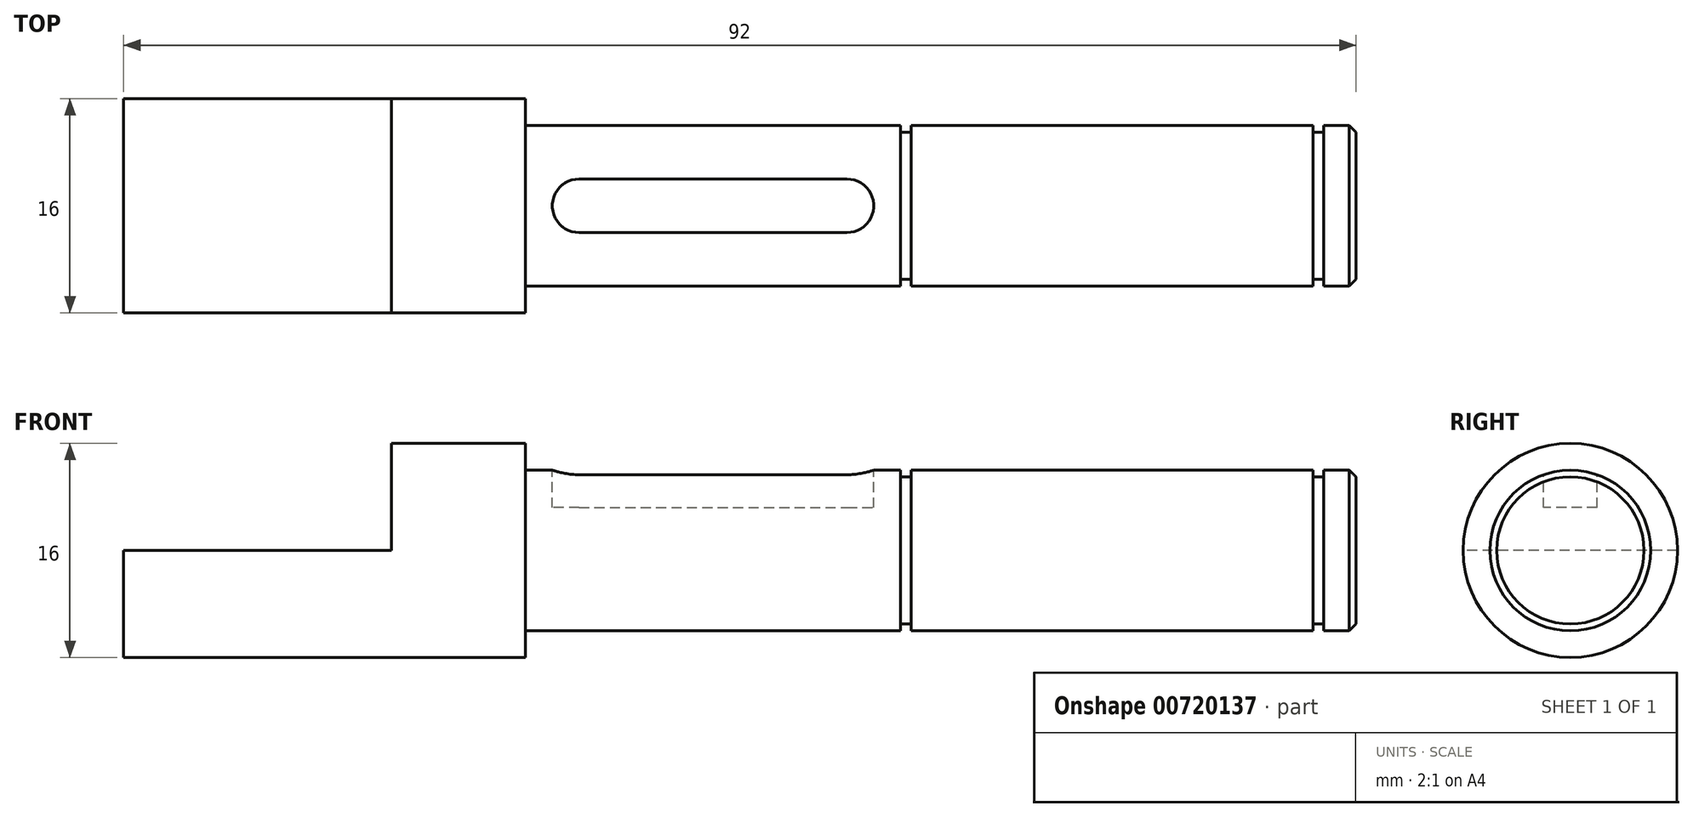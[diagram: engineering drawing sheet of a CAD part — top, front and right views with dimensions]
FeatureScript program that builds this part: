
annotation { "Feature Type Name" : "Feature", "Feature Type Description" : "" }
export const myFeature = defineFeature(function(context is Context, id is Id, definition is map)
    precondition{}
    {
        {
            var Q0;
            Q0=qCreatedBy(makeId("Front.planeOp"),FACE);
            var sketch = newSketch(context, id + "F0", { "sketchPlane" : qUnion([Q0])});
            skLineSegment(sketch, "E0", {"start": v(0, 0) * mm, "end": v(0, 8) * mm});
            skLineSegment(sketch, "E1", {"start": v(0, 8) * mm, "end": v(30, 8) * mm});
            skLineSegment(sketch, "E2", {"start": v(30, 8) * mm, "end": v(30, 6) * mm});
            skLineSegment(sketch, "E3", {"start": v(30, 6) * mm, "end": v(58, 6) * mm});
            skLineSegment(sketch, "E4", {"start": v(92, 6) * mm, "end": v(92, 0) * mm});
            skLineSegment(sketch, "E5", {"start": v(92, 0) * mm, "end": v(0, 0) * mm});
            skLineSegment(sketch, "E6.0", {"start": v(58, 6) * mm, "end": v(58, 5.5) * mm});
            skLineSegment(sketch, "E7.0", {"start": v(58.8, 6) * mm, "end": v(58.8, 5.5) * mm});
            skLineSegment(sketch, "E8.0", {"start": v(88.8, 6) * mm, "end": v(88.8, 5.5) * mm});
            skLineSegment(sketch, "E9.0", {"start": v(89.6, 6) * mm, "end": v(89.6, 5.5) * mm});
            skLineSegment(sketch, "E10.0", {"start": v(58, 5.5) * mm, "end": v(58.8, 5.5) * mm});
            skLineSegment(sketch, "E11.trimOffspring", {"start": v(89.6, 6) * mm, "end": v(92, 6) * mm});
            skLineSegment(sketch, "E12.trimOffspring", {"start": v(58.8, 6) * mm, "end": v(88.8, 6) * mm});
            skLineSegment(sketch, "E13.trimOffspring", {"start": v(88.8, 5.5) * mm, "end": v(89.6, 5.5) * mm});
            skSolve(sketch);
        }
        {
            var Q0;
            Q0=makeQuery(id+"F0.imprint","IMPRINT",FACE,{"disambiguationData":[TD([[makeQuery(id+"F0.imprint","IMPRINT",EDGE,{"derivedFrom":sQuery(id+"F0.wireOp",EDGE,"E0")}),-1.0]])]});
            var Q1;
            Q1=sQuery(id+"F0.wireOp",EDGE,"E5");
            revolve(context, id + "F1", {"surfaceOperationType" : NewSurfaceOperationType.NEW, "entities" : qUnion([Q0]), "axis" : qUnion([Q1]), "revolveType" : RevolveType.FULL});
        }
        {
            var Q0;
            Q0=qCreatedBy(makeId("Top.planeOp"),FACE);
            cPlane(context, id + "F2", {"entities" : qUnion([Q0]), "cplaneType" : CPlaneType.OFFSET, "offset" : 8 * mm, "width" : 150 * mm, "height" : 150 * mm});
        }
        {
            var Q0;
            Q0=qCreatedBy(makeId("Top.planeOp"),FACE);
            cPlane(context, id + "F3", {"entities" : qUnion([Q0]), "cplaneType" : CPlaneType.OFFSET, "offset" : 6 * mm, "width" : 150 * mm, "height" : 150 * mm});
        }
        {
            var Q0;
            Q0=qCreatedBy(id+"F2.planeOp",FACE);
            var sketch = newSketch(context, id + "F4", { "sketchPlane" : qUnion([Q0])});
            skLineSegment(sketch, "E14.bottom", {"start": v(0, 10.44) * mm, "end": v(20, 10.44) * mm});
            skLineSegment(sketch, "E14.top", {"start": v(0, -15.17) * mm, "end": v(20, -15.17) * mm});
            skLineSegment(sketch, "E14.left", {"start": v(0, 10.44) * mm, "end": v(0, -15.17) * mm});
            skLineSegment(sketch, "E14.right", {"start": v(20, 10.44) * mm, "end": v(20, -15.17) * mm});
            skSolve(sketch);
        }
        {
            var Q0;
            Q0=makeQuery(id+"F4.imprint","IMPRINT",FACE,{"disambiguationData":[TD([[makeQuery(id+"F4.imprint","IMPRINT",EDGE,{"derivedFrom":sQuery(id+"F4.wireOp",EDGE,"E14.bottom")}),-1.0]])]});
            extrude(context, id + "F5", {"entities" : qUnion([Q0]), "operationType" : NewBodyOperationType.REMOVE, "oppositeDirection" : true, "depth" : 8 * mm, "offsetDistance" : 25 * mm});
        }
        {
            var Q0;
            Q0=qCreatedBy(id+"F3.planeOp",FACE);
            var sketch = newSketch(context, id + "F6", { "sketchPlane" : qUnion([Q0])});
            skLineSegment(sketch, "E15.bottom", {"start": v(34, 2) * mm, "end": v(54, 2) * mm});
            skLineSegment(sketch, "E15.top", {"start": v(34, -2) * mm, "end": v(54, -2) * mm});
            skLineSegment(sketch, "E15.left", {"start": v(32, 0) * mm, "end": v(32, 0) * mm});
            skLineSegment(sketch, "E15.right", {"start": v(56, 0) * mm, "end": v(56, 0) * mm});
            skPoint(sketch, "E16.visualSharp", {"position": v(32, 2) * mm});
            skArc(sketch, "E16.filletArc", {"start": v(34, 2) * mm, "mid": v(32.59, 1.41) * mm, "end": v(32, 0) * mm});
            skPoint(sketch, "E17.visualSharp", {"position": v(32, -2) * mm});
            skArc(sketch, "E17.filletArc", {"start": v(32, 0) * mm, "mid": v(32.59, -1.41) * mm, "end": v(34, -2) * mm});
            skPoint(sketch, "E18.visualSharp", {"position": v(56, 2) * mm});
            skArc(sketch, "E18.filletArc", {"start": v(56, 0) * mm, "mid": v(55.41, 1.41) * mm, "end": v(54, 2) * mm});
            skPoint(sketch, "E19.visualSharp", {"position": v(56, -2) * mm});
            skArc(sketch, "E19.filletArc", {"start": v(54, -2) * mm, "mid": v(55.41, -1.41) * mm, "end": v(56, 0) * mm});
            skSolve(sketch);
        }
        {
            var Q0;
            Q0=makeQuery(id+"F6.imprint","IMPRINT",FACE,{"disambiguationData":[TD([[makeQuery(id+"F6.imprint","IMPRINT",EDGE,{"derivedFrom":sQuery(id+"F6.wireOp",EDGE,"E15.bottom")}),-1.0]])]});
            extrude(context, id + "F7", {"entities" : qUnion([Q0]), "operationType" : NewBodyOperationType.REMOVE, "oppositeDirection" : true, "depth" : 2.8 * mm, "offsetDistance" : 25 * mm});
        }
        {
            var Q0;
            Q0=makeQuery(id+"F1.opRevolve","SWEPT_EDGE",EDGE,{"disambiguationData":[OSD([sQuery(id+"F0.wireOp",EDGE,"E4"),sQuery(id+"F0.wireOp",EDGE,"E11.trimOffspring")])]});
            chamfer(context, id + "F8", {"entities" : qUnion([Q0]), "width" : .5 * mm, "tangentPropagation" : true});
        }
    });
